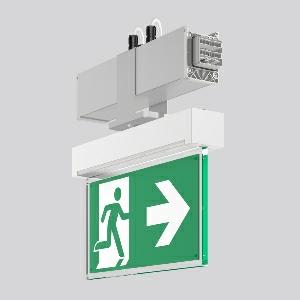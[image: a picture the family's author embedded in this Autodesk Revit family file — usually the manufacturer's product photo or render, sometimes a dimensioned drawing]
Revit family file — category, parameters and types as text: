
# Revit family: linedo_module_rz_9503rz_760_437_030_c52c
name_source: partatom
category: Lighting Fixtures
units: mm (PartAtom-declared; Revit-internal decimal feet)

## family parameters
Cut with Voids When Loaded = No
Host = Face
Light Source = No
Part Type = Normal
Room Calculation Point = No
Round Connector Dimension = Use Diameter
Shared = No

## types (1)
- LINEDO Module RZ
    Apparent Load = 0 VA
    Default Elevation = 1800 mm
    Description = LINEDO, silver, on/off
Continuous line luminaire, L 336 B 62 H 343, SBS, 3 h, DALI-Sibe
    Height = 343 mm
    Lamp = 0 x
    Length = 336 mm
    Luminous efficacy = 0 lm/W
    Manufacturer = RZB
    ModVariant = No
    Model = 9503RZ.760.437.030
    Mounting Place = Ceiling
    Mounting Type = Surface mounted
    Number of Poles = 1
    OnlyDefault = Yes
    Power Factor = 1
    Product Name = LINEDO Module RZ
    Product group = Continuous line luminaire system Linedo IP 54
    ProductGroupID = 314
    Protection Class = Protection class I
    Protection Degree = IP 54
    RLX_Detail_Level = 1
    RLX_Emergency_Light_Flux = 0 lm
    RLX_Emergency_Type = 0
    RLX_Emergency_Type_DB = No
    RlxData = <blob elided: 37473 chars, md5=da66e170>
    Standby Power = 0 W
    System Light Flux = 0 lm
    System Power = 0 W
    Type Comments = Product without accessories
    Type Image = 9503rz.760.434.030.jpg
    URL = http://relux.com
    VarID = ---
    Voltage = 0 V
    Weight = 0.00 kg
    Width = 62 mm  [stored 0.203412 ft]

note: [stored X ft] marks values corroborated as IEEE doubles in the binary element streams (Revit-internal decimal feet)

## geometry (parser evidence)
native form markers: Blend x4, Sweep x10
no freeform markers — native parametric forms only
